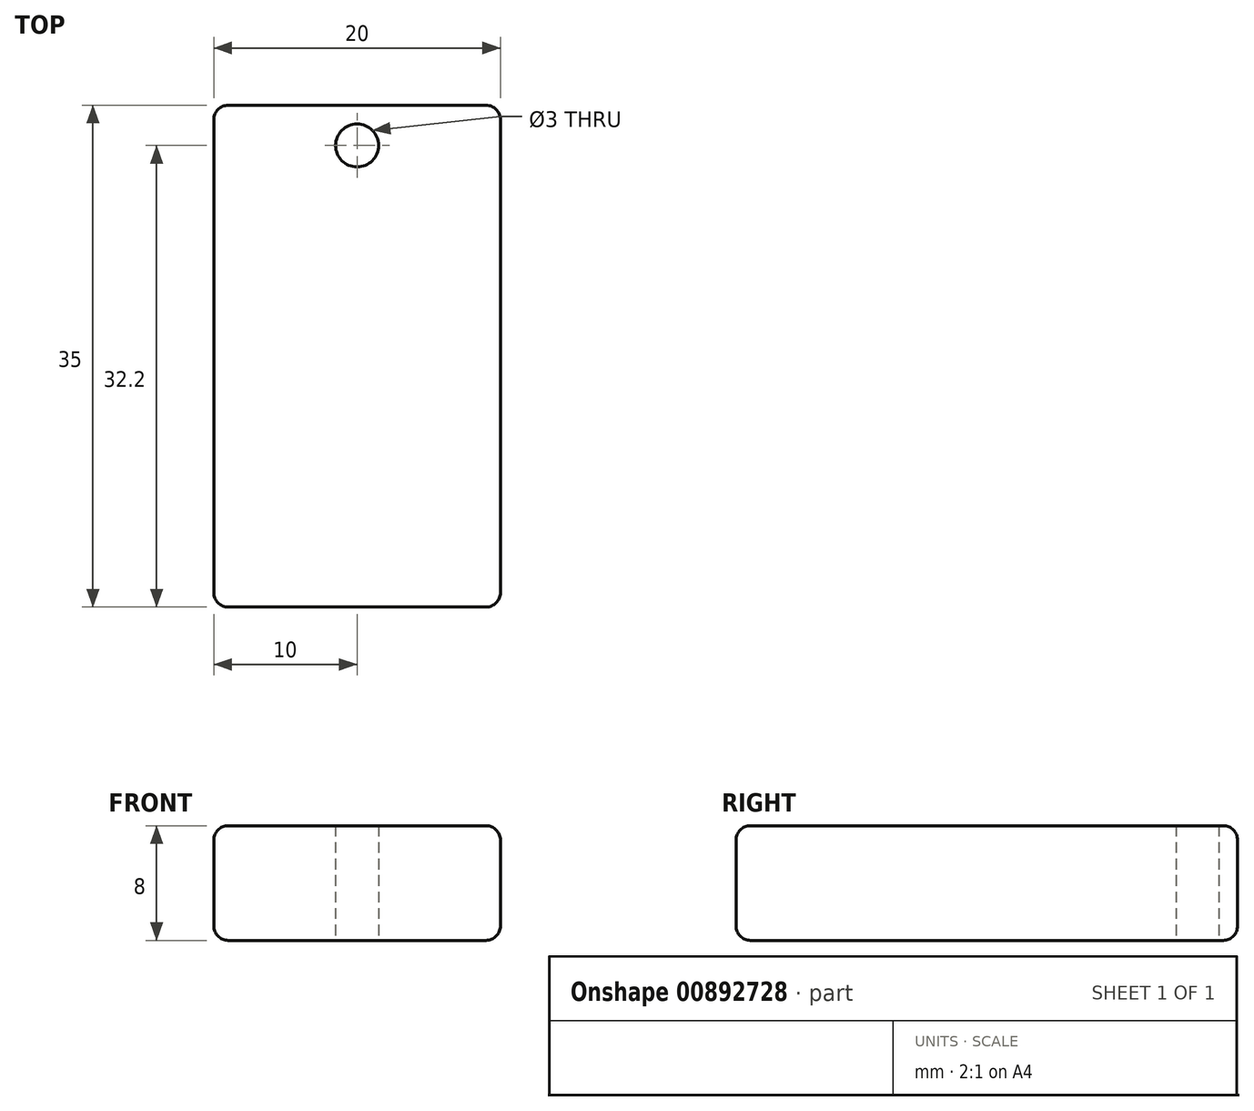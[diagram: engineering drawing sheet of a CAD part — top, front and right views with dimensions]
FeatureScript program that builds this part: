
annotation { "Feature Type Name" : "Feature", "Feature Type Description" : "" }
export const myFeature = defineFeature(function(context is Context, id is Id, definition is map)
    precondition{}
    {
        {
            var Q0;
            Q0=qCreatedBy(makeId("Top.planeOp"),FACE);
            var sketch = newSketch(context, id + "F0", { "sketchPlane" : qUnion([Q0])});
            skLineSegment(sketch, "E0.bottom", {"start": v(10, -17.5) * mm, "end": v(-10, -17.5) * mm});
            skLineSegment(sketch, "E0.top", {"start": v(10, 17.5) * mm, "end": v(-10, 17.5) * mm});
            skLineSegment(sketch, "E0.left", {"start": v(10, -17.5) * mm, "end": v(10, 17.5) * mm});
            skLineSegment(sketch, "E0.right", {"start": v(-10, -17.5) * mm, "end": v(-10, 17.5) * mm});
            skPoint(sketch, "E0.middle", {"position": v(0, 0) * mm});
            skCircle(sketch, "E1", {"center": v(0, 14.7) * mm, "radius": 1.5 * mm});
            skSolve(sketch);
        }
        {
            var Q0;
            Q0=makeQuery(id+"F0.imprint","IMPRINT",FACE,{"disambiguationData":[TD([[makeQuery(id+"F0.imprint","IMPRINT",EDGE,{"derivedFrom":sQuery(id+"F0.wireOp",EDGE,"E0.bottom")}),-1.0]])]});
            extrude(context, id + "F1", {"entities" : qUnion([Q0]), "depth" : 8 * mm, "offsetDistance" : 25 * mm});
        }
        {
            var Q0;
            Q0=makeQuery(id+"F1.opExtrude","CAP_EDGE",EDGE,{"disambiguationData":[OSD([sQuery(id+"F0.wireOp",EDGE,"E0.top")])],"isStart":false});
            var Q1;
            Q1=makeQuery(id+"F1.opExtrude","CAP_EDGE",EDGE,{"disambiguationData":[OSD([sQuery(id+"F0.wireOp",EDGE,"E0.left")])],"isStart":false});
            var Q2;
            Q2=makeQuery(id+"F1.opExtrude","CAP_EDGE",EDGE,{"disambiguationData":[OSD([sQuery(id+"F0.wireOp",EDGE,"E0.right")])],"isStart":false});
            var Q3;
            Q3=makeQuery(id+"F1.opExtrude","CAP_EDGE",EDGE,{"disambiguationData":[OSD([sQuery(id+"F0.wireOp",EDGE,"E0.bottom")])],"isStart":false});
            var Q4;
            Q4=makeQuery(id+"F1.opExtrude","CAP_EDGE",EDGE,{"disambiguationData":[OSD([sQuery(id+"F0.wireOp",EDGE,"E0.right")])],"isStart":true});
            var Q5;
            Q5=makeQuery(id+"F1.opExtrude","SWEPT_EDGE",EDGE,{"disambiguationData":[OSD([sQuery(id+"F0.wireOp",EDGE,"E0.top"),sQuery(id+"F0.wireOp",EDGE,"E0.right")])]});
            var Q6;
            Q6=makeQuery(id+"F1.opExtrude","SWEPT_EDGE",EDGE,{"disambiguationData":[OSD([sQuery(id+"F0.wireOp",EDGE,"E0.bottom"),sQuery(id+"F0.wireOp",EDGE,"E0.right")])]});
            var Q7;
            Q7=makeQuery(id+"F1.opExtrude","CAP_EDGE",EDGE,{"disambiguationData":[OSD([sQuery(id+"F0.wireOp",EDGE,"E0.left")])],"isStart":true});
            var Q8;
            Q8=makeQuery(id+"F1.opExtrude","SWEPT_EDGE",EDGE,{"disambiguationData":[OSD([sQuery(id+"F0.wireOp",EDGE,"E0.top"),sQuery(id+"F0.wireOp",EDGE,"E0.left")])]});
            var Q9;
            Q9=makeQuery(id+"F1.opExtrude","SWEPT_EDGE",EDGE,{"disambiguationData":[OSD([sQuery(id+"F0.wireOp",EDGE,"E0.bottom"),sQuery(id+"F0.wireOp",EDGE,"E0.left")])]});
            var Q10;
            Q10=makeQuery(id+"F1.opExtrude","CAP_EDGE",EDGE,{"disambiguationData":[OSD([sQuery(id+"F0.wireOp",EDGE,"E0.bottom")])],"isStart":true});
            var Q11;
            Q11=makeQuery(id+"F1.opExtrude","CAP_EDGE",EDGE,{"disambiguationData":[OSD([sQuery(id+"F0.wireOp",EDGE,"E0.top")])],"isStart":true});
            fillet(context, id + "F2", {"entities" : qUnion([Q0, Q1, Q2, Q3, Q4, Q5, Q6, Q7, Q8, Q9, Q10, Q11]), "radius" : 1 * mm, "tangentPropagation" : true, "allowEdgeOverflow" : false});
        }
    });
